# Revit family: NU-540 LabGard Class II Type A2 Laminar Flow Biosafety Cabinet with Fixed Rear Seismic Brackets-
name_source: partatom
category: Mechanical Equipment
units: mm (PartAtom-declared; Revit-internal decimal feet)

## family parameters
Always vertical = Yes
Cut with Voids When Loaded = No
OmniClass Number = 23.75.00.00
OmniClass Title = Climate Control (HVAC)
Part Type = Normal
Room Calculation Point = No
Round Connector Dimension = Use Diameter
Shared = No
Work Plane-Based = No

## types (4) — shared parameters
Default Elevation = 0' - 0"

## per-type parameters (varying)
| type | Bracket Spacing | Cabinet Width | Exhaust Filter Width | Overall Width | Unistrut Length | Workzone Width | crossbar | window width |
| NU-540-600 | 5' - 3 5/16" | 5' - 10 9/16" | 2' - 10 1/2" | 6' - 5 9/16" | 5' - 7 9/16" | 5' - 10 3/8" | 5' - 10 5/32" | 5' - 11 7/8" |
| NU-540-500 | 4' - 3 5/16" | 4' - 10 9/16" | 2' - 4 1/2" | 5' - 5 9/16" | 4' - 8 11/16" | 4' - 10 3/8" | 4' - 10 5/32" | 4' - 11 7/8" |
| NU-540-400 | 3' - 3 5/16" | 3' - 10 9/16" | 1' - 8 1/2" | 4' - 5 9/16" | 3' - 8 11/16" | 3' - 10 3/8" | 3' - 10 5/32" | 3' - 11 3/8" |
| NU-540-300 | 2' - 3 5/16" | 2' - 10 9/16" | 1' - 0 1/2" | 3' - 5 9/16" | 2' - 8 11/16" | 2' - 10 3/8" | 2' - 10 5/32" | 2' - 11 7/8" |

## geometry (parser evidence)
native form markers: Sweep x7
no freeform markers — native parametric forms only
